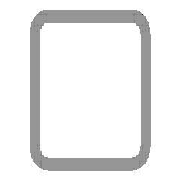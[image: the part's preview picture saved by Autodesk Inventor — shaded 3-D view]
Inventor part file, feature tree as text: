
AUTODESK INVENTOR PART (.ipt)
format: ipt  version: 2025 (Build 290162010, 162A)  size: 134,656 bytes
history: native  units: mm (DEFAULTED — no unit token found)
features: other x4, sketch x1, plane x1
ambient origin geometry x8: Origin, YZ Plane, XZ Plane, XY Plane, X Axis, Y Axis, Z Axis, Center Point
bodies: Solid1 (feature_tree), Body (feature_tree)
feature tree (6):
  parser-record x1  (decoder bookkeeping rows leaked as tree rows — omitted from the tree; the rows remain in map.json)
  other  "Driven Length"
  other  "Start Plane"
  other  "End Plane"
  sketch  "Sketch3"  dims[d3=1359.696742mm d4=0.0mm d7=6.0mm d9=80.0mm d11=80.0mm d12=3.0mm d13=40.0mm d14=1399.696742mm d15=40.0mm d16=40.0mm d17=90.0deg d18=1359.696742mm]
  plane  "Work Plane3"
